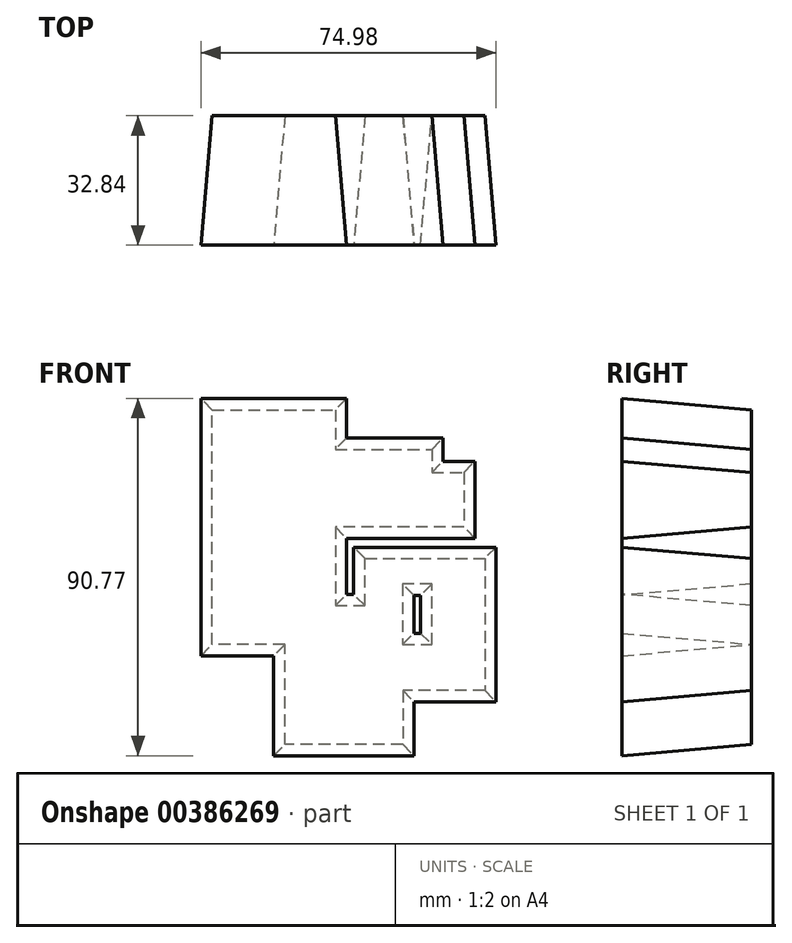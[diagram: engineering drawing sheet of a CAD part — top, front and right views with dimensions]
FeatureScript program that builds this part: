
annotation { "Feature Type Name" : "Feature", "Feature Type Description" : "" }
export const myFeature = defineFeature(function(context is Context, id is Id, definition is map)
    precondition{}
    {
        {
            var Q0;
            Q0=qCreatedBy(makeId("Front.planeOp"),FACE);
            var sketch = newSketch(context, id + "F0", { "sketchPlane" : qUnion([Q0])});
            skLineSegment(sketch, "E0.bottom", {"start": v(0, 15.34) * mm, "end": v(-7.42, 15.34) * mm});
            skLineSegment(sketch, "E0.top", {"start": v(0, 0) * mm, "end": v(-7.42, 0) * mm});
            skLineSegment(sketch, "E0.left", {"start": v(0, 15.34) * mm, "end": v(0, 0) * mm});
            skLineSegment(sketch, "E0.right", {"start": v(-7.42, 15.34) * mm, "end": v(-7.42, 0) * mm});
            skLineSegment(sketch, "E1.bottom", {"start": v(-24.53, 0) * mm, "end": v(-55.8, 0) * mm});
            skLineSegment(sketch, "E1.top", {"start": v(-24.53, 59.64) * mm, "end": v(-55.8, 59.64) * mm});
            skLineSegment(sketch, "E1.left", {"start": v(-24.53, 0) * mm, "end": v(-24.53, 59.64) * mm});
            skLineSegment(sketch, "E1.right", {"start": v(-55.8, 0) * mm, "end": v(-55.8, 59.64) * mm});
            skLineSegment(sketch, "E2.bottom", {"start": v(0, 49.6) * mm, "end": v(-24.53, 49.6) * mm});
            skLineSegment(sketch, "E2.top", {"start": v(0, 37.8) * mm, "end": v(-24.53, 37.8) * mm});
            skLineSegment(sketch, "E2.left", {"start": v(0, 49.6) * mm, "end": v(0, 37.8) * mm});
            skLineSegment(sketch, "E2.right", {"start": v(-24.53, 49.6) * mm, "end": v(-24.53, 37.8) * mm});
            skPoint(sketch, "E3.firstSnap0", {"position": v(0, 43.7) * mm});
            skPoint(sketch, "E3.oppositeSnap0", {"position": v(-24.53, 29.82) * mm});
            skLineSegment(sketch, "E3.bottom", {"start": v(8.12, 43.7) * mm, "end": v(-35.72, 43.7) * mm});
            skLineSegment(sketch, "E3.top", {"start": v(8.12, 29.82) * mm, "end": v(-35.72, 29.82) * mm});
            skLineSegment(sketch, "E3.left", {"start": v(8.12, 43.7) * mm, "end": v(8.12, 29.82) * mm});
            skLineSegment(sketch, "E3.right", {"start": v(-35.72, 43.7) * mm, "end": v(-35.72, 29.82) * mm});
            skLineSegment(sketch, "E4.bottom", {"start": v(-16.98, 21.85) * mm, "end": v(13.43, 21.85) * mm});
            skLineSegment(sketch, "E4.top", {"start": v(-16.98, -11.66) * mm, "end": v(13.43, -11.66) * mm});
            skLineSegment(sketch, "E4.left", {"start": v(-16.98, 21.85) * mm, "end": v(-16.98, -11.66) * mm});
            skLineSegment(sketch, "E4.right", {"start": v(13.43, 21.85) * mm, "end": v(13.43, -11.66) * mm});
            skLineSegment(sketch, "E5.bottom", {"start": v(-37.35, 9.9) * mm, "end": v(-7.38, 9.9) * mm});
            skLineSegment(sketch, "E5.top", {"start": v(-37.35, -25.4) * mm, "end": v(-7.38, -25.4) * mm});
            skLineSegment(sketch, "E5.left", {"start": v(-37.35, 9.9) * mm, "end": v(-37.35, -25.4) * mm});
            skLineSegment(sketch, "E5.right", {"start": v(-7.38, 9.9) * mm, "end": v(-7.38, -25.4) * mm});
            skSolve(sketch);
        }
        {
            var Q0;
            {var subQ0=sQuery(id+"F0.wireOp",EDGE,"E1.left");var subQ1=sQuery(id+"F0.wireOp",EDGE,"E1.bottom");var subQ2=makeQuery(id+"F0.imprint","INTERSECT",VERTEX,{"derivedFrom":[subQ1,subQ0]});Q0=makeQuery(id+"F0.imprint","IMPRINT",FACE,{"disambiguationData":[TD([[makeQuery(id+"F0.imprint","IMPRINT",EDGE,{"disambiguationData":[TD([[subQ2,-1.0]])],"derivedFrom":subQ1}),-1.0]])]});}
            var Q1;
            {var subQ7=sQuery(id+"F0.wireOp",EDGE,"E0.right");var subQ8=sQuery(id+"F0.wireOp",EDGE,"E0.top");var subQ9=makeQuery(id+"F0.imprint","INTERSECT",VERTEX,{"derivedFrom":[subQ8,subQ7]});Q1=makeQuery(id+"F0.imprint","IMPRINT",FACE,{"disambiguationData":[TD([[makeQuery(id+"F0.imprint","IMPRINT",EDGE,{"disambiguationData":[TD([[subQ9,1.0]])],"derivedFrom":subQ8}),1.0]])]});}
            var Q2;
            {var subQ1=sQuery(id+"F0.wireOp",EDGE,"E2.top");Q2=makeQuery(id+"F0.imprint","IMPRINT",FACE,{"disambiguationData":[TD([[makeQuery(id+"F0.imprint","IMPRINT",EDGE,{"derivedFrom":subQ1}),1.0]])]});}
            var Q3;
            {var subQ0=sQuery(id+"F0.wireOp",EDGE,"E2.top");Q3=makeQuery(id+"F0.imprint","IMPRINT",FACE,{"disambiguationData":[TD([[makeQuery(id+"F0.imprint","IMPRINT",EDGE,{"derivedFrom":subQ0}),-1.0]])]});}
            var Q4;
            {var subQ0=sQuery(id+"F0.wireOp",EDGE,"E2.bottom");Q4=makeQuery(id+"F0.imprint","IMPRINT",FACE,{"disambiguationData":[TD([[makeQuery(id+"F0.imprint","IMPRINT",EDGE,{"derivedFrom":subQ0}),1.0]])]});}
            var Q5;
            {var subQ1=sQuery(id+"F0.wireOp",EDGE,"E0.bottom");Q5=makeQuery(id+"F0.imprint","IMPRINT",FACE,{"disambiguationData":[TD([[makeQuery(id+"F0.imprint","IMPRINT",EDGE,{"derivedFrom":subQ1}),-1.0]])]});}
            var Q6;
            {var subQ10=sQuery(id+"F0.wireOp",EDGE,"E5.top");Q6=makeQuery(id+"F0.imprint","IMPRINT",FACE,{"disambiguationData":[TD([[makeQuery(id+"F0.imprint","IMPRINT",EDGE,{"derivedFrom":subQ10}),1.0]])]});}
            var Q7;
            {var subQ0=sQuery(id+"F0.wireOp",EDGE,"E3.right");Q7=makeQuery(id+"F0.imprint","IMPRINT",FACE,{"disambiguationData":[TD([[makeQuery(id+"F0.imprint","IMPRINT",EDGE,{"derivedFrom":subQ0}),1.0]])]});}
            var Q8;
            {var subQ15=sQuery(id+"F0.wireOp",EDGE,"E1.top");Q8=makeQuery(id+"F0.imprint","IMPRINT",FACE,{"disambiguationData":[TD([[makeQuery(id+"F0.imprint","IMPRINT",EDGE,{"derivedFrom":subQ15}),1.0]])]});}
            extrude(context, id + "F1", {"entities" : qUnion([Q0, Q1, Q2, Q3, Q4, Q5, Q6, Q7, Q8]), "depth" : 32.84 * mm, "hasDraft" : true, "draftAngle" : 5 * degree});
        }
    });
